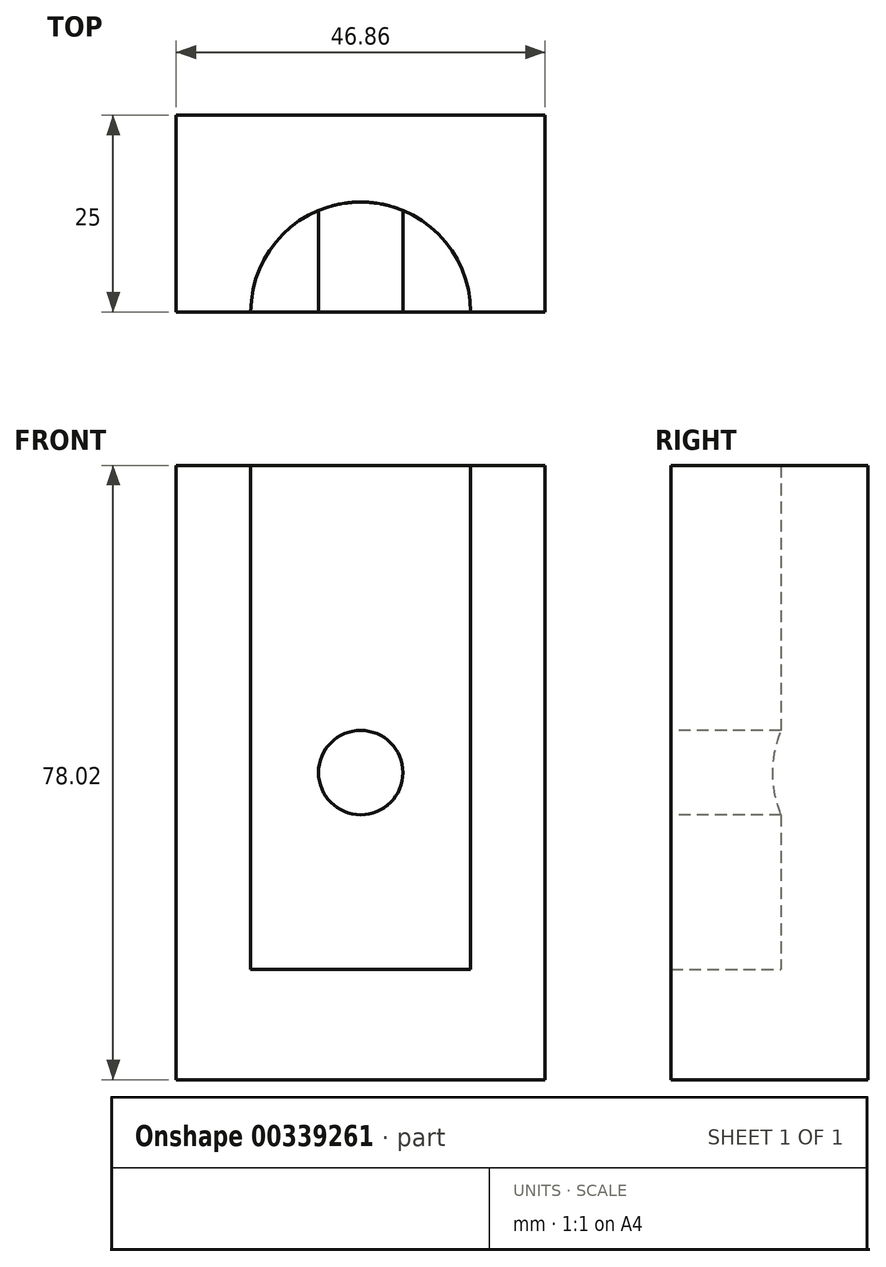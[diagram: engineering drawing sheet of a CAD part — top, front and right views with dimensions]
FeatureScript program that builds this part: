
annotation { "Feature Type Name" : "Feature", "Feature Type Description" : "" }
export const myFeature = defineFeature(function(context is Context, id is Id, definition is map)
    precondition{}
    {
        {
            var Q0;
            Q0=qCreatedBy(makeId("Front.planeOp"),FACE);
            var sketch = newSketch(context, id + "F0", { "sketchPlane" : qUnion([Q0])});
            skLineSegment(sketch, "E0.bottom", {"start": v(-23.43, 39.01) * mm, "end": v(23.43, 39.01) * mm});
            skLineSegment(sketch, "E0.top", {"start": v(-23.43, -39.01) * mm, "end": v(23.43, -39.01) * mm});
            skLineSegment(sketch, "E0.left", {"start": v(-23.43, 39.01) * mm, "end": v(-23.43, -39.01) * mm});
            skLineSegment(sketch, "E0.right", {"start": v(23.43, 39.01) * mm, "end": v(23.43, -39.01) * mm});
            skSolve(sketch);
        }
        {
            var Q0;
            Q0=makeQuery(id+"F0.imprint","IMPRINT",FACE,{"disambiguationData":[TD([[makeQuery(id+"F0.imprint","IMPRINT",EDGE,{"derivedFrom":sQuery(id+"F0.wireOp",EDGE,"E0.bottom")}),-1.0]])]});
            extrude(context, id + "F1", {"entities" : qUnion([Q0]), "oppositeDirection" : true, "depth" : 25 * mm});
        }
        {
            var Q0;
            Q0=qCreatedBy(makeId("Top.planeOp"),FACE);
            var sketch = newSketch(context, id + "F2", { "sketchPlane" : qUnion([Q0])});
            skCircle(sketch, "E1", {"center": v(0, 0) * mm, "radius": 13.97 * mm});
            skSolve(sketch);
        }
        {
            var Q0;
            Q0=makeQuery(id+"F2.imprint","IMPRINT",FACE,{"disambiguationData":[TD([[makeQuery(id+"F2.imprint","IMPRINT",EDGE,{"derivedFrom":sQuery(id+"F2.wireOp",EDGE,"E1")}),1.0]])]});
            extrude(context, id + "F3", {"entities" : qUnion([Q0]), "operationType" : NewBodyOperationType.REMOVE, "depth" : 42.8 * mm, "hasSecondDirection" : true, "secondDirectionOppositeDirection" : true, "secondDirectionDepth" : 25 * mm});
        }
        {
            var Q0;
            Q0=qCreatedBy(makeId("Front.planeOp"),FACE);
            var sketch = newSketch(context, id + "F4", { "sketchPlane" : qUnion([Q0])});
            skCircle(sketch, "E2", {"center": v(0, 0) * mm, "radius": 5.36 * mm});
            skSolve(sketch);
        }
        {
            var Q0;
            Q0=makeQuery(id+"F4.imprint","IMPRINT",FACE,{"disambiguationData":[TD([[makeQuery(id+"F4.imprint","IMPRINT",EDGE,{"derivedFrom":sQuery(id+"F4.wireOp",EDGE,"E2")}),1.0]])]});
            extrude(context, id + "F5", {"entities" : qUnion([Q0]), "operationType" : NewBodyOperationType.ADD, "oppositeDirection" : true, "depth" : 22.4 * mm});
        }
    });
